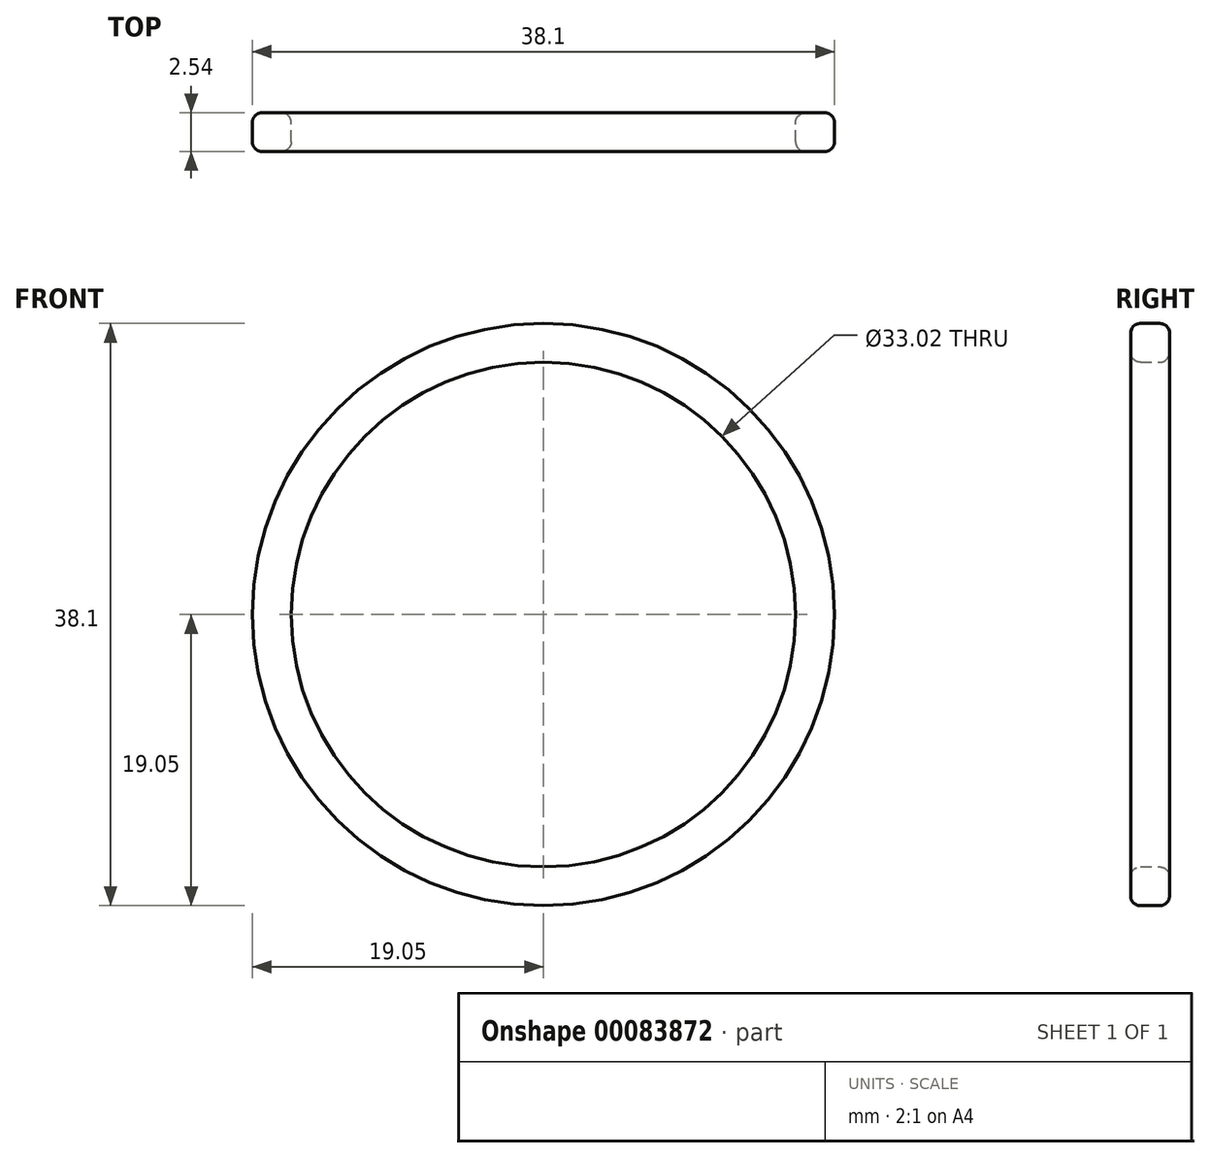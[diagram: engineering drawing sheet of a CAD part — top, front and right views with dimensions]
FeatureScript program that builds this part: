
annotation { "Feature Type Name" : "Feature", "Feature Type Description" : "" }
export const myFeature = defineFeature(function(context is Context, id is Id, definition is map)
    precondition{}
    {
        {
            var Q0;
            Q0=qCreatedBy(makeId("Front.planeOp"),FACE);
            var sketch = newSketch(context, id + "F0", { "sketchPlane" : qUnion([Q0])});
            skCircle(sketch, "E0", {"center": v(0, 0) * mm, "radius": 19.05 * mm});
            skCircle(sketch, "E1", {"center": v(0, 0) * mm, "radius": 16.51 * mm});
            skSolve(sketch);
        }
        {
            var Q0;
            Q0=makeQuery(id+"F0.imprint","IMPRINT",FACE,{"disambiguationData":[TD([[makeQuery(id+"F0.imprint","IMPRINT",EDGE,{"derivedFrom":sQuery(id+"F0.wireOp",EDGE,"E0")}),1.0]])]});
            extrude(context, id + "F1", {"entities" : qUnion([Q0]), "depth" : 2.54 * mm});
        }
        {
            var Q0;
            Q0=makeQuery(id+"F1.opExtrude","CAP_EDGE",EDGE,{"disambiguationData":[OSD([sQuery(id+"F0.wireOp",EDGE,"E1")])],"isStart":true});
            var Q1;
            Q1=makeQuery(id+"F1.opExtrude","CAP_EDGE",EDGE,{"disambiguationData":[OSD([sQuery(id+"F0.wireOp",EDGE,"E0")])],"isStart":true});
            fillet(context, id + "F2", {"entities" : qUnion([Q0, Q1]), "radius" : 0.64 * mm, "tangentPropagation" : true, "allowEdgeOverflow" : false});
        }
        {
            var Q0;
            Q0=makeQuery(id+"F1.opExtrude","CAP_EDGE",EDGE,{"disambiguationData":[OSD([sQuery(id+"F0.wireOp",EDGE,"E1")])],"isStart":false});
            var Q1;
            Q1=makeQuery(id+"F1.opExtrude","CAP_EDGE",EDGE,{"disambiguationData":[OSD([sQuery(id+"F0.wireOp",EDGE,"E0")])],"isStart":false});
            fillet(context, id + "F3", {"entities" : qUnion([Q0, Q1]), "radius" : 0.64 * mm, "tangentPropagation" : true, "allowEdgeOverflow" : false});
        }
    });
